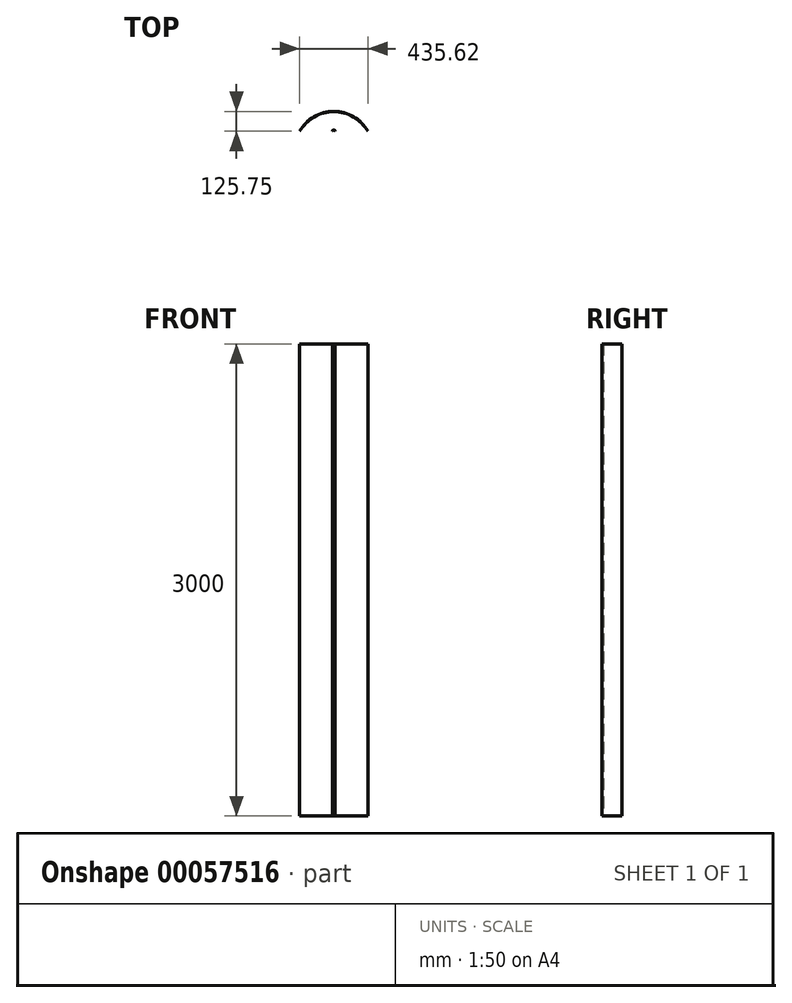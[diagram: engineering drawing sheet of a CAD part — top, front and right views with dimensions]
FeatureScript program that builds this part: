
annotation { "Feature Type Name" : "Feature", "Feature Type Description" : "" }
export const myFeature = defineFeature(function(context is Context, id is Id, definition is map)
    precondition{}
    {
        {
            var Q0;
            Q0=qCreatedBy(makeId("Top.planeOp"),FACE);
            var sketch = newSketch(context, id + "F0", { "sketchPlane" : qUnion([Q0])});
            skArc(sketch, "E0", {"start": v(216.07, 125.75) * mm, "mid": v(0, 250) * mm, "end": v(-216.07, 125.75) * mm});
            skArc(sketch, "E1.0", {"start": v(217.8, 125.75) * mm, "mid": v(0, 251.5) * mm, "end": v(-217.8, 125.75) * mm});
            skLineSegment(sketch, "E2", {"start": v(-251.5, 0) * mm, "end": v(-250, 0) * mm});
            skLineSegment(sketch, "E3.trimOffspring", {"start": v(250, 0) * mm, "end": v(251.5, 0) * mm});
            skPoint(sketch, "E4", {"position": v(0, 125.75) * mm});
            skLineSegment(sketch, "E5", {"start": v(-217.8, 125.75) * mm, "end": v(-216.07, 125.75) * mm});
            skCircle(sketch, "E6", {"center": v(0, 125.75) * mm, "radius": 7.5 * mm});
            skCircle(sketch, "E7.0", {"center": v(0, 125.75) * mm, "radius": 8.5 * mm});
            skLineSegment(sketch, "E8.trimOffspring", {"start": v(216.07, 125.75) * mm, "end": v(217.8, 125.75) * mm});
            skLineSegment(sketch, "E9.trimOffspring", {"start": v(-8.5, 125.75) * mm, "end": v(8.5, 125.75) * mm});
            skSolve(sketch);
        }
        {
            var Q0;
            Q0=makeQuery(id+"F0.imprint","IMPRINT",FACE,{"disambiguationData":[TD([[makeQuery(id+"F0.imprint","IMPRINT",EDGE,{"derivedFrom":sQuery(id+"F0.wireOp",EDGE,"E0")}),-1.0]])]});
            extrude(context, id + "F1", {"entities" : qUnion([Q0]), "depth" : 3000 * mm});
        }
        {
            var Q0;
            Q0=makeQuery(id+"F0.imprint","IMPRINT",FACE,{"disambiguationData":[TD([[makeQuery(id+"F0.imprint","IMPRINT",EDGE,{"derivedFrom":sQuery(id+"F0.wireOp",EDGE,"E0")}),-1.0]])]});
            var Q1;
            {var subQ0=sQuery(id+"F0.wireOp",EDGE,"E9.trimOffspring");var subQ1=sQuery(id+"F0.wireOp",EDGE,"E6");var subQ2=makeQuery(id+"F0.imprint","INTERSECT",VERTEX,{"disambiguationData":[OD(0.0)],"derivedFrom":[subQ1,subQ0]});Q1=makeQuery(id+"F0.imprint","IMPRINT",FACE,{"disambiguationData":[TD([[makeQuery(id+"F0.imprint","IMPRINT",EDGE,{"disambiguationData":[TD([[subQ2,1.0]])],"derivedFrom":subQ1}),-1.0]])]});}
            extrude(context, id + "F2", {"entities" : qUnion([Q0, Q1]), "depth" : 3000 * mm});
        }
    });
